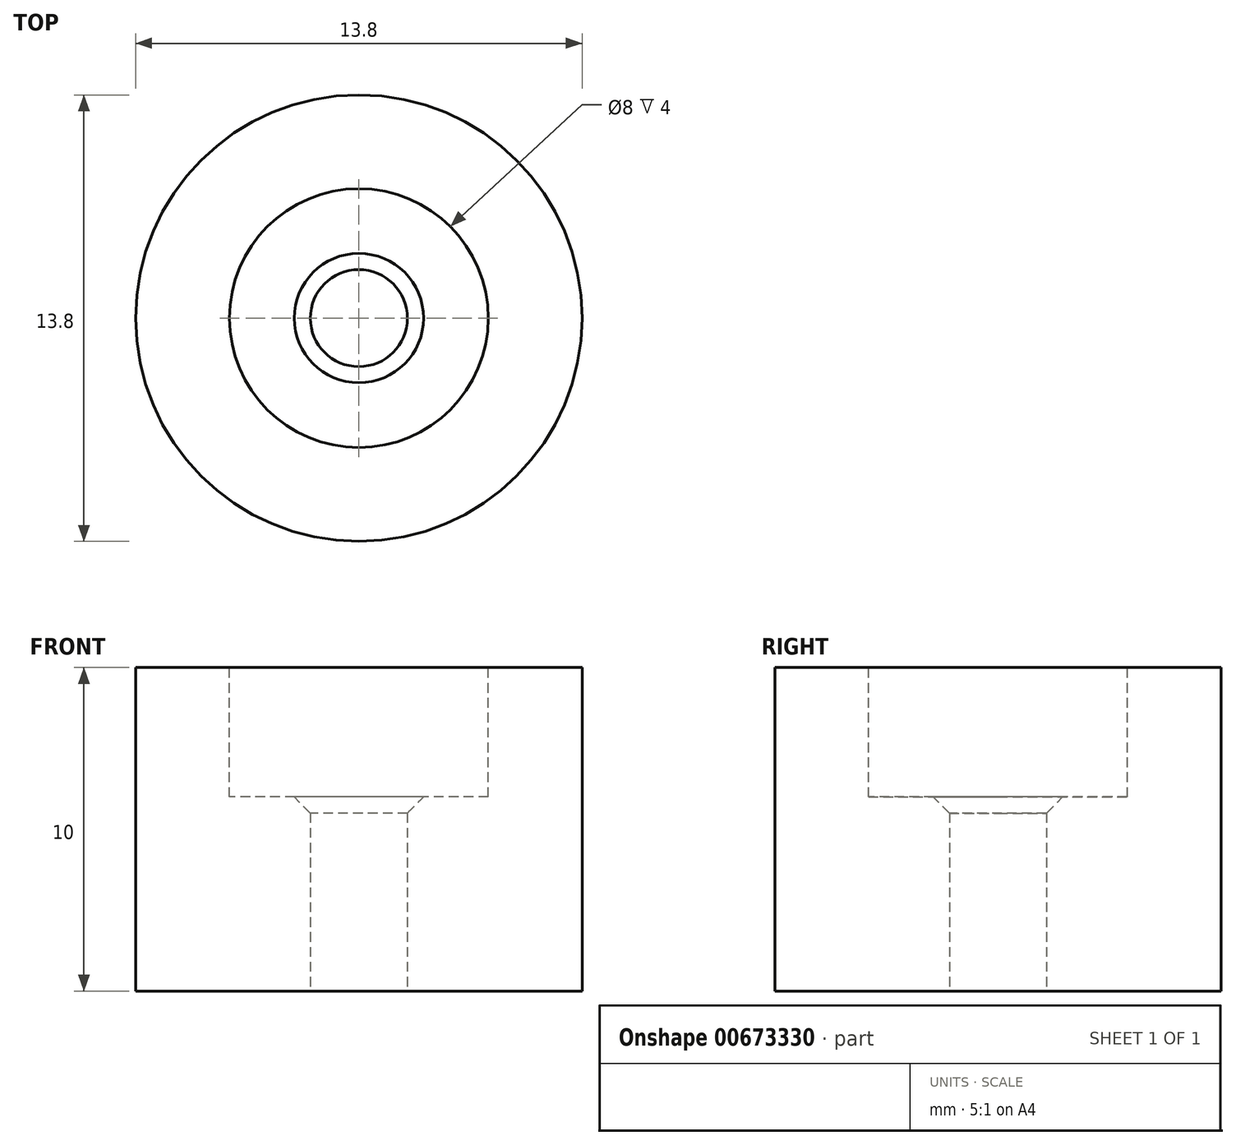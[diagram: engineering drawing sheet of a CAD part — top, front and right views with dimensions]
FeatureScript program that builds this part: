
annotation { "Feature Type Name" : "Feature", "Feature Type Description" : "" }
export const myFeature = defineFeature(function(context is Context, id is Id, definition is map)
    precondition{}
    {
        {
            var Q0;
            Q0=qCreatedBy(makeId("Top.planeOp"),FACE);
            var sketch = newSketch(context, id + "F0", { "sketchPlane" : qUnion([Q0])});
            skCircle(sketch, "E0", {"center": v(0, 0) * mm, "radius": 6.9 * mm});
            skCircle(sketch, "E1", {"center": v(0, 0) * mm, "radius": 1.5 * mm});
            skSolve(sketch);
        }
        {
            var Q0;
            Q0=makeQuery(id+"F0.imprint","IMPRINT",FACE,{"disambiguationData":[TD([[makeQuery(id+"F0.imprint","IMPRINT",EDGE,{"derivedFrom":sQuery(id+"F0.wireOp",EDGE,"E0")}),1.0]])]});
            extrude(context, id + "F1", {"entities" : qUnion([Q0]), "depth" : 10 * mm, "offsetDistance" : 25 * mm});
        }
        {
            var Q0;
            Q0=makeQuery(id+"F1.opExtrude","CAP_FACE",FACE,{"disambiguationData":[OSD([sQuery(id+"F0.wireOp",EDGE,"E0"),sQuery(id+"F0.wireOp",EDGE,"E1")])],"isStart":false});
            var sketch = newSketch(context, id + "F2", { "sketchPlane" : qUnion([Q0])});
            skCircle(sketch, "E2", {"center": v(0, 0) * mm, "radius": 4 * mm});
            skSolve(sketch);
        }
        {
            var Q0;
            Q0 = qSketchRegion(id + "F2", true);
            extrude(context, id + "F3", {"entities" : qUnion([Q0]), "operationType" : NewBodyOperationType.REMOVE, "oppositeDirection" : true, "depth" : 4 * mm, "offsetDistance" : 25 * mm});
        }
        {
            var Q0;
            Q0=makeQuery(id+"F3.boolean.opBoolean","INTERSECT",EDGE,{"derivedFrom":[makeQuery(id+"F1.opExtrude","SWEPT_FACE",FACE,{"disambiguationData":[OSD([sQuery(id+"F0.wireOp",EDGE,"E1")])]}),makeQuery(id+"F3.opExtrude","CAP_FACE",FACE,{"disambiguationData":[OSD([sQuery(id+"F2.wireOp",EDGE,"E2")])],"isStart":false})]});
            chamfer(context, id + "F4", {"entities" : qUnion([Q0]), "width" : 0.5 * mm, "tangentPropagation" : true});
        }
    });
